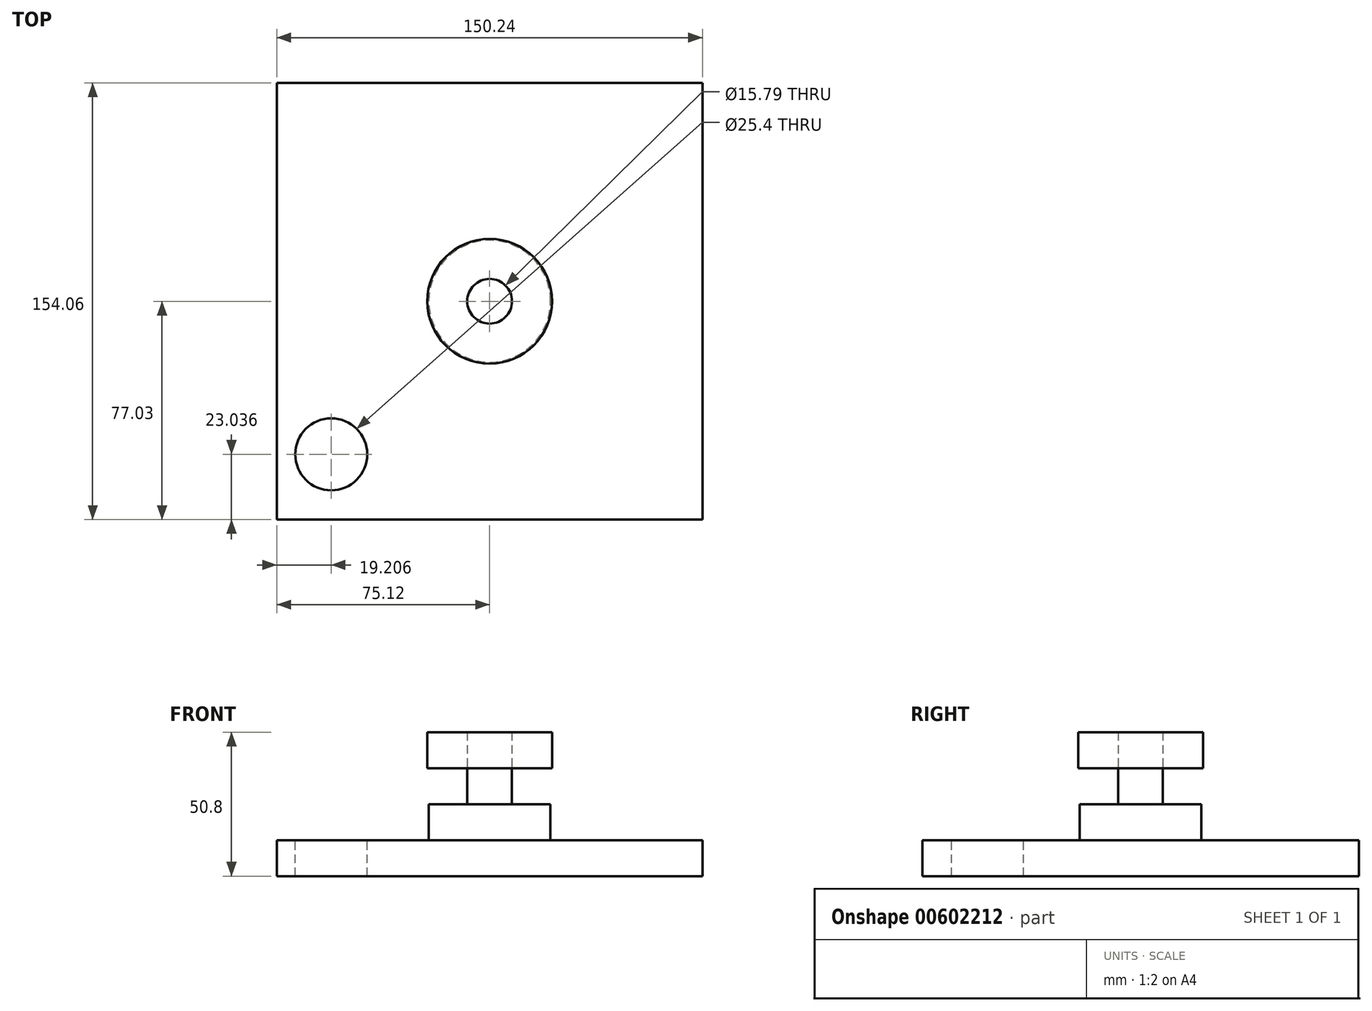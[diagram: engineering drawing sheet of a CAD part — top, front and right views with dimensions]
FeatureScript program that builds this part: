
annotation { "Feature Type Name" : "Feature", "Feature Type Description" : "" }
export const myFeature = defineFeature(function(context is Context, id is Id, definition is map)
    precondition{}
    {
        {
            var Q0;
            Q0=qCreatedBy(makeId("Top.planeOp"),FACE);
            var sketch = newSketch(context, id + "F0", { "sketchPlane" : qUnion([Q0])});
            skCircle(sketch, "E0", {"center": v(0, 0) * mm, "radius": 21.47 * mm});
            skSolve(sketch);
        }
        {
            var Q0;
            Q0=makeQuery(id+"F0.imprint","IMPRINT",FACE,{"disambiguationData":[TD([[makeQuery(id+"F0.imprint","IMPRINT",EDGE,{"derivedFrom":sQuery(id+"F0.wireOp",EDGE,"E0")}),1.0]])]});
            extrude(context, id + "F1", {"entities" : qUnion([Q0]), "depth" : 25.4 * mm, "offsetDistance" : 25.4 * mm});
        }
        {
            var Q0;
            Q0=qCreatedBy(makeId("Top.planeOp"),FACE);
            var sketch = newSketch(context, id + "F2", { "sketchPlane" : qUnion([Q0])});
            skLineSegment(sketch, "E1.bottom", {"start": v(75.12, 77.03) * mm, "end": v(-75.12, 77.03) * mm});
            skLineSegment(sketch, "E1.top", {"start": v(75.12, -77.03) * mm, "end": v(-75.12, -77.03) * mm});
            skLineSegment(sketch, "E1.left", {"start": v(75.12, 77.03) * mm, "end": v(75.12, -77.03) * mm});
            skLineSegment(sketch, "E1.right", {"start": v(-75.12, 77.03) * mm, "end": v(-75.12, -77.03) * mm});
            skPoint(sketch, "E1.middle", {"position": v(0, 0) * mm});
            skSolve(sketch);
        }
        {
            var Q0;
            Q0=makeQuery(id+"F2.imprint","IMPRINT",FACE,{"disambiguationData":[TD([[makeQuery(id+"F2.imprint","IMPRINT",EDGE,{"derivedFrom":sQuery(id+"F2.wireOp",EDGE,"E1.bottom")}),1.0]])]});
            extrude(context, id + "F3", {"entities" : qUnion([Q0]), "operationType" : NewBodyOperationType.ADD, "depth" : 12.7 * mm, "offsetDistance" : 25.4 * mm});
        }
        {
            var Q0;
            Q0=makeQuery(id+"F1.opExtrude","CAP_FACE",FACE,{"disambiguationData":[OSD([sQuery(id+"F0.wireOp",EDGE,"E0")])],"isStart":false});
            var sketch = newSketch(context, id + "F4", { "sketchPlane" : qUnion([Q0])});
            skCircle(sketch, "E2", {"center": v(0, 0) * mm, "radius": 7.9 * mm});
            skSolve(sketch);
        }
        {
            var Q0;
            Q0=makeQuery(id+"F4.imprint","IMPRINT",FACE,{"disambiguationData":[TD([[makeQuery(id+"F4.imprint","IMPRINT",EDGE,{"derivedFrom":sQuery(id+"F4.wireOp",EDGE,"E2")}),1.0]])]});
            extrude(context, id + "F5", {"entities" : qUnion([Q0]), "operationType" : NewBodyOperationType.ADD, "depth" : 12.7 * mm, "offsetDistance" : 25.4 * mm});
        }
        {
            var Q0;
            Q0=makeQuery(id+"F5.opExtrude","CAP_FACE",FACE,{"disambiguationData":[OSD([sQuery(id+"F4.wireOp",EDGE,"E2")])],"isStart":false});
            var sketch = newSketch(context, id + "F6", { "sketchPlane" : qUnion([Q0])});
            skCircle(sketch, "E3", {"center": v(0, 0) * mm, "radius": 22.02 * mm});
            skSolve(sketch);
        }
        {
            var Q0;
            Q0=makeQuery(id+"F6.imprint","IMPRINT",FACE,{"disambiguationData":[TD([[makeQuery(id+"F6.imprint","IMPRINT",EDGE,{"derivedFrom":sQuery(id+"F6.wireOp",EDGE,"E3")}),1.0]])]});
            extrude(context, id + "F7", {"entities" : qUnion([Q0]), "depth" : 12.7 * mm, "offsetDistance" : 25.4 * mm});
        }
        {
            var Q0;
            Q0=makeQuery(id+"F3.opExtrude","CAP_FACE",FACE,{"disambiguationData":[OSD([sQuery(id+"F2.wireOp",EDGE,"E1.bottom"),sQuery(id+"F2.wireOp",EDGE,"E1.top"),sQuery(id+"F2.wireOp",EDGE,"E1.left"),sQuery(id+"F2.wireOp",EDGE,"E1.right")])],"isStart":false});
            var sketch = newSketch(context, id + "F8", { "sketchPlane" : qUnion([Q0])});
            skCircle(sketch, "E4", {"center": v(-55.91, -54) * mm, "radius": 13.81 * mm});
            skPoint(sketch, "E4.first.point", {"position": v(-63.63, -42.54) * mm});
            skPoint(sketch, "E4.second.point", {"position": v(-46, -63.6) * mm});
            skPoint(sketch, "E4.third.point", {"position": v(-67.35, -46.25) * mm});
            skSolve(sketch);
        }
        {
            var Q0;
            Q0=sQuery(id+"F8.wireOp",VERTEX,"E4.center");
            var Q1;
            Q1=makeQuery(id+"F1.opExtrude","SWEPT_BODY",BODY,{"disambiguationData":[OSD([sQuery(id+"F0.wireOp",EDGE,"E0")])]});
            hole(context, id + "F9", {"style" : HoleStyle.SIMPLE, "endStyle" : HoleEndStyle.BLIND, "holeDiameter" : 25.4 * mm, "majorDiameter" : 6.35 * mm, "holeDepth" : 25.4 * mm, "isTappedThrough" : true, "tappedDepth" : 12.7 * mm, "tapClearance" : 3, "startFromSketch" : true, "locations" : qUnion([Q0]), "scope" : qUnion([Q1])});
        }
    });
